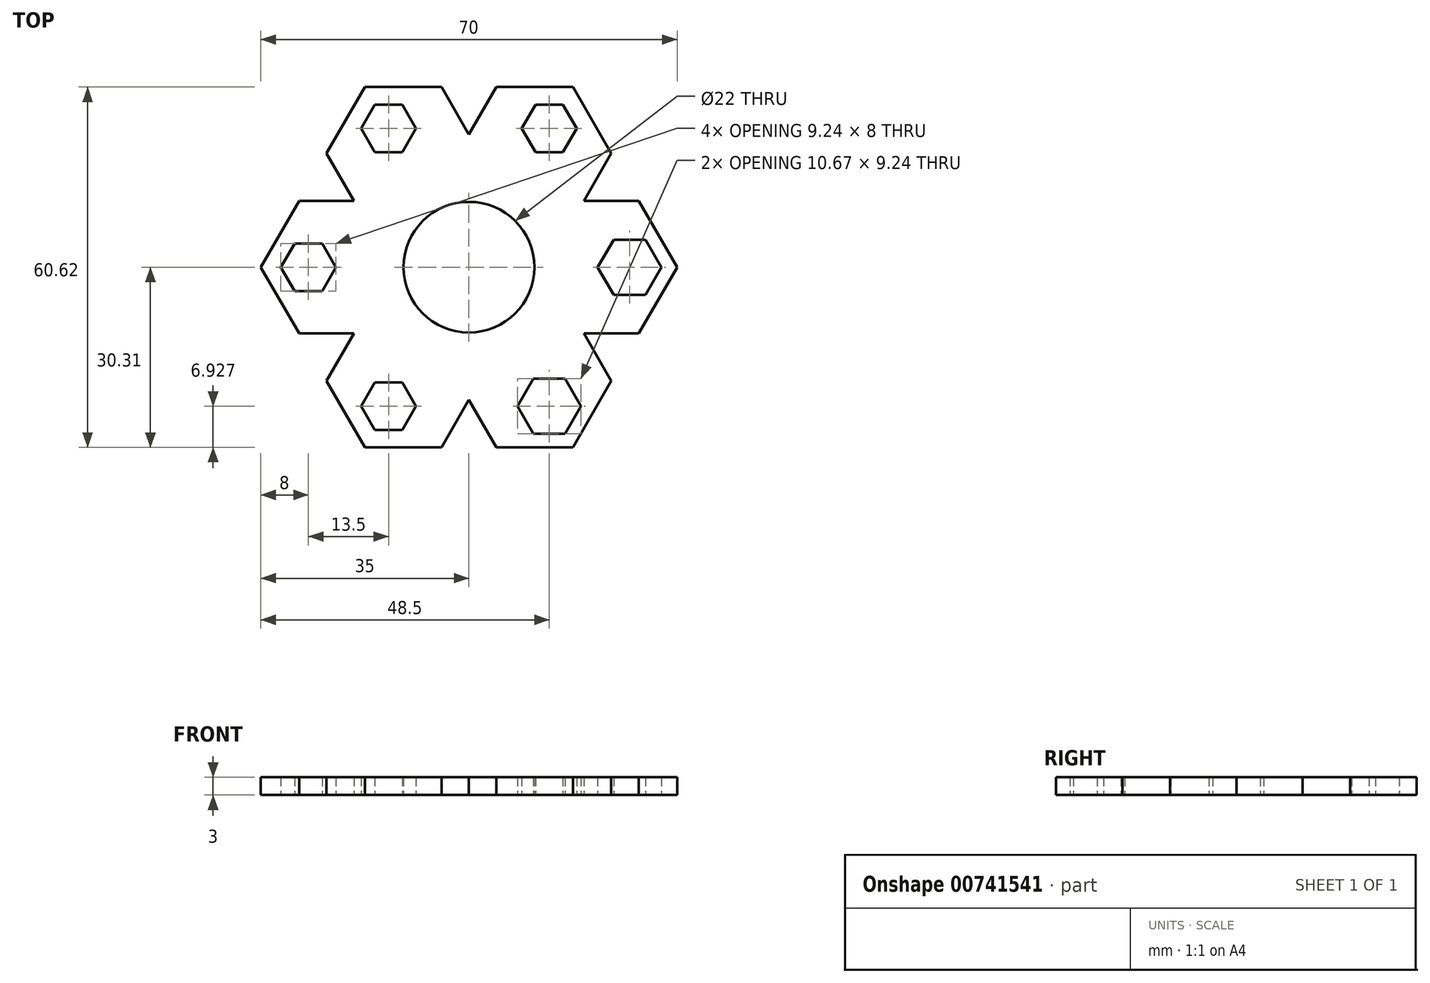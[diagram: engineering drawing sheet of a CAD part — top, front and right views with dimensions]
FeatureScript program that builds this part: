
annotation { "Feature Type Name" : "Feature", "Feature Type Description" : "" }
export const myFeature = defineFeature(function(context is Context, id is Id, definition is map)
    precondition{}
    {
        {
            var Q0;
            Q0=qCreatedBy(makeId("Top.planeOp"),FACE);
            var sketch = newSketch(context, id + "F0", { "sketchPlane" : qUnion([Q0])});
            skPoint(sketch, "E0.center", {"position": v(0, 0) * mm});
            skCircle(sketch, "E1", {"center": v(0, 0) * mm, "radius": 11 * mm});
            skLineSegment(sketch, "E2.0", {"start": v(17.5, -30.31) * mm, "end": v(4.62, -30.31) * mm});
            skLineSegment(sketch, "E2.1", {"start": v(-17.5, -30.31) * mm, "end": v(-23.94, -19.16) * mm});
            skLineSegment(sketch, "E2.2", {"start": v(-35, 0) * mm, "end": v(-28.56, 11.16) * mm});
            skLineSegment(sketch, "E2.3", {"start": v(-17.5, 30.31) * mm, "end": v(-4.62, 30.31) * mm});
            skLineSegment(sketch, "E2.4", {"start": v(17.5, 30.31) * mm, "end": v(23.94, 19.16) * mm});
            skLineSegment(sketch, "E2.5", {"start": v(35, 0) * mm, "end": v(28.56, -11.16) * mm});
            skLineSegment(sketch, "E3.0", {"start": v(-18.12, 23.38) * mm, "end": v(-15.8, 27.38) * mm});
            skLineSegment(sketch, "E3.1", {"start": v(-15.8, 27.38) * mm, "end": v(-11.2, 27.38) * mm});
            skLineSegment(sketch, "E3.2", {"start": v(-11.2, 27.38) * mm, "end": v(-8.88, 23.38) * mm});
            skLineSegment(sketch, "E3.3", {"start": v(-8.88, 23.38) * mm, "end": v(-11.2, 19.38) * mm});
            skLineSegment(sketch, "E3.4", {"start": v(-11.2, 19.38) * mm, "end": v(-15.8, 19.38) * mm});
            skLineSegment(sketch, "E3.5", {"start": v(-15.8, 19.38) * mm, "end": v(-18.12, 23.38) * mm});
            skLineSegment(sketch, "E4.0", {"start": v(-31.62, 0) * mm, "end": v(-29.3, 4) * mm});
            skLineSegment(sketch, "E4.1", {"start": v(-29.3, 4) * mm, "end": v(-24.7, 4) * mm});
            skLineSegment(sketch, "E4.2", {"start": v(-24.7, 4) * mm, "end": v(-22.38, 0) * mm});
            skLineSegment(sketch, "E4.3", {"start": v(-22.38, 0) * mm, "end": v(-24.7, -4) * mm});
            skLineSegment(sketch, "E4.4", {"start": v(-24.7, -4) * mm, "end": v(-29.3, -4) * mm});
            skLineSegment(sketch, "E4.5", {"start": v(-29.3, -4) * mm, "end": v(-31.62, 0) * mm});
            skLineSegment(sketch, "E5.0", {"start": v(-8.88, -23.38) * mm, "end": v(-11.2, -27.38) * mm});
            skLineSegment(sketch, "E5.1", {"start": v(-11.2, -27.38) * mm, "end": v(-15.8, -27.38) * mm});
            skLineSegment(sketch, "E5.2", {"start": v(-15.8, -27.38) * mm, "end": v(-18.12, -23.38) * mm});
            skLineSegment(sketch, "E5.3", {"start": v(-18.12, -23.38) * mm, "end": v(-15.8, -19.38) * mm});
            skLineSegment(sketch, "E5.4", {"start": v(-15.8, -19.38) * mm, "end": v(-11.2, -19.38) * mm});
            skLineSegment(sketch, "E5.5", {"start": v(-11.2, -19.38) * mm, "end": v(-8.88, -23.38) * mm});
            skLineSegment(sketch, "E6.0", {"start": v(16.17, -18.76) * mm, "end": v(18.83, -23.38) * mm});
            skLineSegment(sketch, "E6.1", {"start": v(18.83, -23.38) * mm, "end": v(16.17, -28) * mm});
            skLineSegment(sketch, "E6.2", {"start": v(16.17, -28) * mm, "end": v(10.83, -28) * mm});
            skLineSegment(sketch, "E6.3", {"start": v(10.83, -28) * mm, "end": v(8.17, -23.38) * mm});
            skLineSegment(sketch, "E6.4", {"start": v(8.17, -23.38) * mm, "end": v(10.83, -18.76) * mm});
            skLineSegment(sketch, "E6.5", {"start": v(10.83, -18.76) * mm, "end": v(16.17, -18.76) * mm});
            skLineSegment(sketch, "E7.0", {"start": v(32.33, 0) * mm, "end": v(29.67, -4.62) * mm});
            skLineSegment(sketch, "E7.1", {"start": v(29.67, -4.62) * mm, "end": v(24.33, -4.62) * mm});
            skLineSegment(sketch, "E7.2", {"start": v(24.33, -4.62) * mm, "end": v(21.67, 0) * mm});
            skLineSegment(sketch, "E7.3", {"start": v(21.67, 0) * mm, "end": v(24.33, 4.62) * mm});
            skLineSegment(sketch, "E7.4", {"start": v(24.33, 4.62) * mm, "end": v(29.67, 4.62) * mm});
            skLineSegment(sketch, "E7.5", {"start": v(29.67, 4.62) * mm, "end": v(32.33, 0) * mm});
            skLineSegment(sketch, "E8.0", {"start": v(15.8, 19.38) * mm, "end": v(11.2, 19.38) * mm});
            skLineSegment(sketch, "E8.1", {"start": v(11.2, 19.38) * mm, "end": v(8.88, 23.38) * mm});
            skLineSegment(sketch, "E8.2", {"start": v(8.88, 23.38) * mm, "end": v(11.2, 27.38) * mm});
            skLineSegment(sketch, "E8.3", {"start": v(11.2, 27.38) * mm, "end": v(15.8, 27.38) * mm});
            skLineSegment(sketch, "E8.4", {"start": v(15.8, 27.38) * mm, "end": v(18.12, 23.38) * mm});
            skLineSegment(sketch, "E8.5", {"start": v(18.12, 23.38) * mm, "end": v(15.8, 19.38) * mm});
            skLineSegment(sketch, "E9", {"start": v(-19.32, -11.16) * mm, "end": v(-23.94, -19.16) * mm});
            skLineSegment(sketch, "E10", {"start": v(-19.32, -11.16) * mm, "end": v(-28.56, -11.16) * mm});
            skLineSegment(sketch, "E11", {"start": v(0, -22.31) * mm, "end": v(4.62, -30.31) * mm});
            skLineSegment(sketch, "E12", {"start": v(0, -22.31) * mm, "end": v(-4.62, -30.31) * mm});
            skLineSegment(sketch, "E13", {"start": v(19.32, -11.16) * mm, "end": v(23.94, -19.16) * mm});
            skLineSegment(sketch, "E14", {"start": v(19.32, -11.16) * mm, "end": v(28.56, -11.16) * mm});
            skLineSegment(sketch, "E15", {"start": v(19.32, 11.16) * mm, "end": v(23.94, 19.16) * mm});
            skLineSegment(sketch, "E16", {"start": v(19.32, 11.16) * mm, "end": v(28.56, 11.16) * mm});
            skLineSegment(sketch, "E17", {"start": v(0, 22.31) * mm, "end": v(-4.62, 30.31) * mm});
            skLineSegment(sketch, "E18", {"start": v(0, 22.31) * mm, "end": v(4.62, 30.31) * mm});
            skLineSegment(sketch, "E19", {"start": v(-19.32, 11.16) * mm, "end": v(-23.94, 19.16) * mm});
            skLineSegment(sketch, "E20", {"start": v(-19.32, 11.16) * mm, "end": v(-28.56, 11.16) * mm});
            skLineSegment(sketch, "E21.trimOffspring", {"start": v(-23.94, 19.16) * mm, "end": v(-17.5, 30.31) * mm});
            skLineSegment(sketch, "E22.trimOffspring", {"start": v(4.62, 30.31) * mm, "end": v(17.5, 30.31) * mm});
            skLineSegment(sketch, "E23.trimOffspring", {"start": v(28.56, 11.16) * mm, "end": v(35, 0) * mm});
            skLineSegment(sketch, "E24.trimOffspring", {"start": v(23.94, -19.16) * mm, "end": v(17.5, -30.31) * mm});
            skLineSegment(sketch, "E25.trimOffspring", {"start": v(-4.62, -30.31) * mm, "end": v(-17.5, -30.31) * mm});
            skLineSegment(sketch, "E26.trimOffspring", {"start": v(-28.56, -11.16) * mm, "end": v(-35, 0) * mm});
            skSolve(sketch);
        }
        {
            var Q0;
            Q0 = qSketchRegion(id + "F0", true);
            extrude(context, id + "F1", {"entities" : qUnion([Q0]), "depth" : 3 * mm, "offsetDistance" : 25 * mm});
        }
    });
